# Revit family: RSP-900
name_source: partatom
category: Furniture
units: mm (PartAtom-declared; Revit-internal decimal feet)

## family parameters
Always vertical = Yes
Cut with Voids When Loaded = No
OmniClass Number = 23.40.20.00
OmniClass Title = General Furniture and Specialties
Room Calculation Point = No
Shared = No
Work Plane-Based = No

## types (6) — shared parameters
Default Elevation = 0"
ES Seat Count = 1
Frame = Chair, Kendo, Black-90
Frame seat = Steel ASTM A572
HS Seat Count = 1
Steel = Steel, Chrome Plated

## per-type parameters (varying)
| type | Decorate | Seat |
| RSP-900-BLU | Chair, Kendo, Blue | Chair, Kendo, THEATER |
| RSP-900-WHT | Chair, Kendo, WHITE | Chair, Kendo, THEATER |
| RSP-900-GRY | Chair, Kendo, GRAY | Chair, Kendo, THEATER |
| RSP-900-RED | Chair, Kendo, RED | Chair, Kendo, THEATER |
| RSP-900F-GRY | Chair, Kendo, THEATER | Chair, Kendo, GRAY FABRIC |
| RSP-900-BLK | Chair, Kendo, THEATER | Chair, Kendo, THEATER |

note: column(s) folded — value = type name in every type: Model

## geometry (parser evidence)
native form markers: Sweep x11
no freeform markers — native parametric forms only
